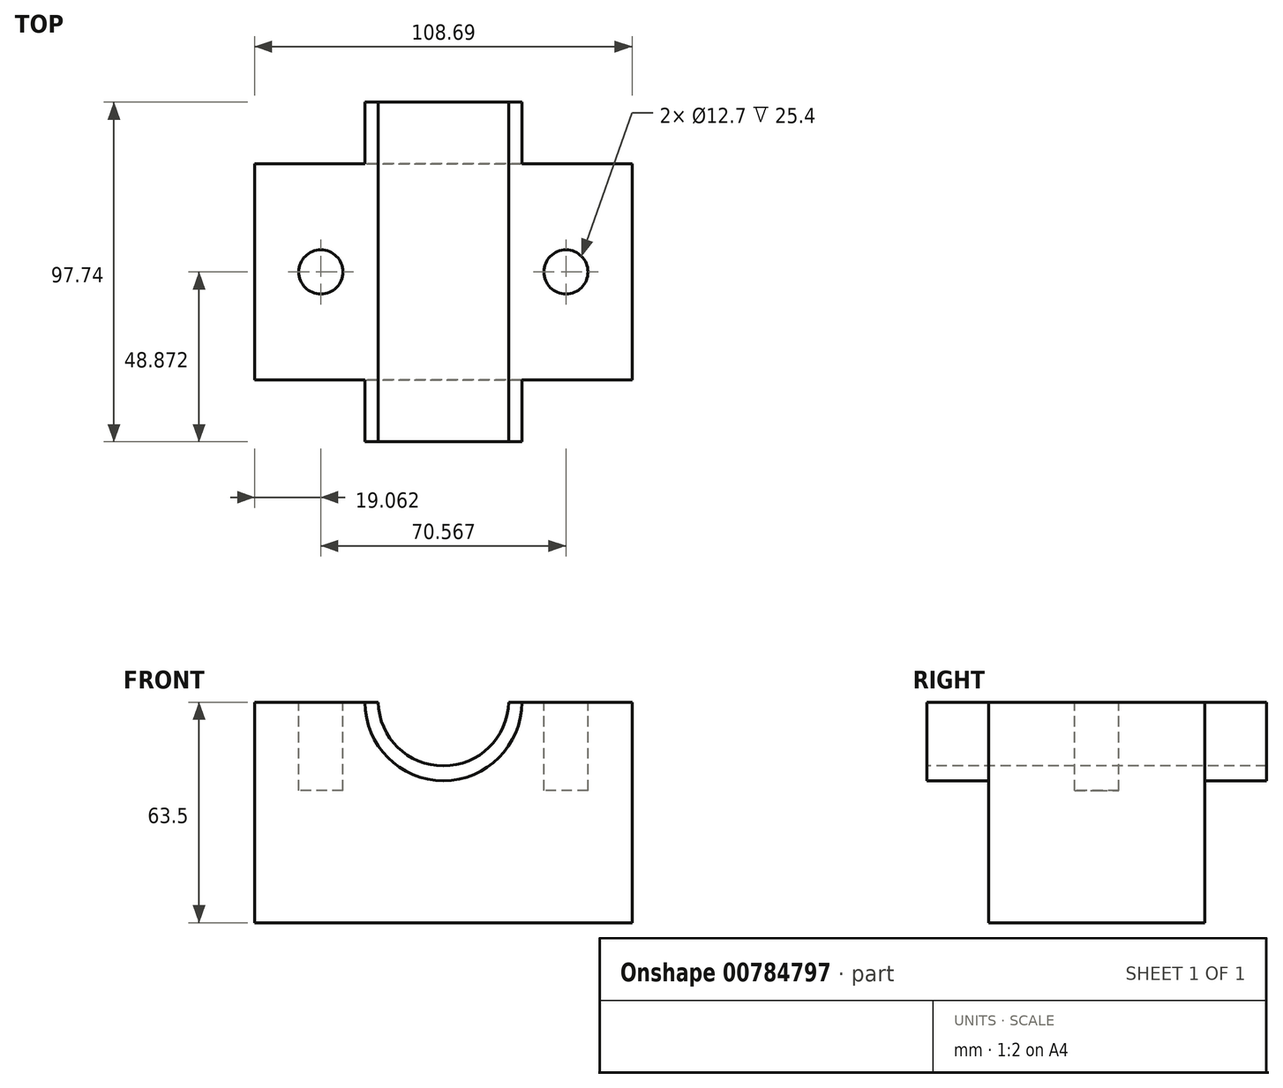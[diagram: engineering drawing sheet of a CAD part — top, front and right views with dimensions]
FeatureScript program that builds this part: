
annotation { "Feature Type Name" : "Feature", "Feature Type Description" : "" }
export const myFeature = defineFeature(function(context is Context, id is Id, definition is map)
    precondition{}
    {
        {
            var Q0;
            Q0=qCreatedBy(makeId("Top.planeOp"),FACE);
            var sketch = newSketch(context, id + "F0", { "sketchPlane" : qUnion([Q0])});
            skLineSegment(sketch, "E0.bottom", {"start": v(-52.9, 29.04) * mm, "end": v(55.8, 29.04) * mm});
            skLineSegment(sketch, "E0.top", {"start": v(-52.9, -33.14) * mm, "end": v(55.8, -33.14) * mm});
            skLineSegment(sketch, "E0.left", {"start": v(-52.9, 29.04) * mm, "end": v(-52.9, -33.14) * mm});
            skLineSegment(sketch, "E0.right", {"start": v(55.8, 29.04) * mm, "end": v(55.8, -33.14) * mm});
            skSolve(sketch);
        }
        {
            var Q0;
            Q0=makeQuery(id+"F0.imprint","IMPRINT",FACE,{"disambiguationData":[TD([[makeQuery(id+"F0.imprint","IMPRINT",EDGE,{"derivedFrom":sQuery(id+"F0.wireOp",EDGE,"E0.bottom")}),-1.0]])]});
            extrude(context, id + "F1", {"entities" : qUnion([Q0]), "depth" : 63.5 * mm, "offsetDistance" : 25.4 * mm});
        }
        {
            var Q0;
            Q0=makeQuery(id+"F1.opExtrude","CAP_FACE",FACE,{"disambiguationData":[OSD([sQuery(id+"F0.wireOp",EDGE,"E0.bottom"),sQuery(id+"F0.wireOp",EDGE,"E0.top"),sQuery(id+"F0.wireOp",EDGE,"E0.left"),sQuery(id+"F0.wireOp",EDGE,"E0.right")])],"isStart":false});
            var sketch = newSketch(context, id + "F2", { "sketchPlane" : qUnion([Q0])});
            skLineSegment(sketch, "E1", {"start": v(-52.9, -2.05) * mm, "end": v(-40.19, -2.05) * mm, "construction": true});
            skCircle(sketch, "E2", {"center": v(-33.84, -2.05) * mm, "radius": 6.35 * mm});
            skCircle(sketch, "E3", {"center": v(36.73, -2.05) * mm, "radius": 6.35 * mm});
            skLineSegment(sketch, "E4.trimOffspring", {"start": v(-33.84, -2.05) * mm, "end": v(36.73, -2.05) * mm, "construction": true});
            skLineSegment(sketch, "E5.trimOffspring", {"start": v(43.08, -2.05) * mm, "end": v(55.8, -2.05) * mm, "construction": true});
            skSolve(sketch);
        }
        {
            var Q0;
            Q0=makeQuery(id+"F2.imprint","IMPRINT",FACE,{"disambiguationData":[TD([[makeQuery(id+"F2.imprint","IMPRINT",EDGE,{"derivedFrom":sQuery(id+"F2.wireOp",EDGE,"E2")}),1.0]])]});
            var Q1;
            Q1=makeQuery(id+"F2.imprint","IMPRINT",FACE,{"disambiguationData":[TD([[makeQuery(id+"F2.imprint","IMPRINT",EDGE,{"derivedFrom":sQuery(id+"F2.wireOp",EDGE,"E3")}),1.0]])]});
            extrude(context, id + "F3", {"entities" : qUnion([Q0, Q1]), "operationType" : NewBodyOperationType.REMOVE, "oppositeDirection" : true, "depth" : 25.4 * mm, "offsetDistance" : 25.4 * mm});
        }
        {
            var Q0;
            Q0=makeQuery(id+"F1.opExtrude","CAP_FACE",FACE,{"disambiguationData":[OSD([sQuery(id+"F0.wireOp",EDGE,"E0.bottom"),sQuery(id+"F0.wireOp",EDGE,"E0.top"),sQuery(id+"F0.wireOp",EDGE,"E0.left"),sQuery(id+"F0.wireOp",EDGE,"E0.right")])],"isStart":false});
            var sketch = newSketch(context, id + "F4", { "sketchPlane" : qUnion([Q0])});
            skLineSegment(sketch, "E6", {"start": v(-21.15, -33.14) * mm, "end": v(-21.15, 29.04) * mm});
            skLineSegment(sketch, "E7", {"start": v(-21.15, 29.04) * mm, "end": v(-21.15, 46.82) * mm});
            skLineSegment(sketch, "E8", {"start": v(-21.15, 46.82) * mm, "end": v(24.04, 46.82) * mm});
            skLineSegment(sketch, "E9", {"start": v(24.04, 46.82) * mm, "end": v(24.04, -50.92) * mm});
            skLineSegment(sketch, "E10", {"start": v(24.04, -50.92) * mm, "end": v(-21.15, -50.92) * mm});
            skLineSegment(sketch, "E11", {"start": v(-21.15, -50.92) * mm, "end": v(-21.15, -33.14) * mm});
            skSolve(sketch);
        }
        {
            var Q0;
            {var subQ0=sQuery(id+"F4.wireOp",EDGE,"E10");Q0=makeQuery(id+"F4.imprint","IMPRINT",FACE,{"disambiguationData":[TD([[makeQuery(id+"F4.imprint","IMPRINT",EDGE,{"derivedFrom":subQ0}),-1.0]])]});}
            var Q1;
            {var subQ0=sQuery(id+"F4.wireOp",EDGE,"E6");Q1=makeQuery(id+"F4.imprint","IMPRINT",FACE,{"disambiguationData":[TD([[makeQuery(id+"F4.imprint","IMPRINT",EDGE,{"derivedFrom":subQ0}),-1.0]])]});}
            var Q2;
            {var subQ0=sQuery(id+"F4.wireOp",EDGE,"E7");Q2=makeQuery(id+"F4.imprint","IMPRINT",FACE,{"disambiguationData":[TD([[makeQuery(id+"F4.imprint","IMPRINT",EDGE,{"derivedFrom":subQ0}),-1.0]])]});}
            extrude(context, id + "F5", {"entities" : qUnion([Q0, Q1, Q2]), "operationType" : NewBodyOperationType.ADD, "oppositeDirection" : true, "depth" : 25.4 * mm, "offsetDistance" : 25.4 * mm});
        }
        {
            var Q0;
            Q0=makeQuery(id+"F5.opExtrude","SWEPT_FACE",FACE,{"disambiguationData":[OSD([sQuery(id+"F4.wireOp",EDGE,"E10")])]});
            var sketch = newSketch(context, id + "F6", { "sketchPlane" : qUnion([Q0])});
            skArc(sketch, "E12", {"start": v(-21.15, 63.5) * mm, "mid": v(1.45, 40.9) * mm, "end": v(24.04, 63.5) * mm});
            skPoint(sketch, "E13", {"position": v(-17.34, 63.5) * mm});
            skPoint(sketch, "E14", {"position": v(20.23, 63.5) * mm});
            skArc(sketch, "E15", {"start": v(-17.34, 63.5) * mm, "mid": v(1.45, 45.17) * mm, "end": v(20.23, 63.5) * mm});
            skSolve(sketch);
        }
        {
            var Q0;
            Q0=makeQuery(id+"F6.imprint","IMPRINT",FACE,{"disambiguationData":[TD([[makeQuery(id+"F6.imprint","IMPRINT",EDGE,{"derivedFrom":sQuery(id+"F6.wireOp",EDGE,"E12")}),-1.0]])]});
            var Q1;
            Q1=makeQuery(id+"F1.opExtrude","SWEPT_FACE",FACE,{"disambiguationData":[OSD([sQuery(id+"F0.wireOp",EDGE,"E0.top")])]});
            extrude(context, id + "F7", {"entities" : qUnion([Q0]), "operationType" : NewBodyOperationType.REMOVE, "endBound" : BoundingType.UP_TO_SURFACE, "oppositeDirection" : true, "depth" : 25.4 * mm, "endBoundEntityFace" : qUnion([Q1]), "offsetDistance" : 25.4 * mm});
        }
        {
            var Q0;
            Q0=makeQuery(id+"F5.opExtrude","SWEPT_FACE",FACE,{"disambiguationData":[OSD([sQuery(id+"F4.wireOp",EDGE,"E10")])]});
            var sketch = newSketch(context, id + "F8", { "sketchPlane" : qUnion([Q0])});
            skPoint(sketch, "E16", {"position": v(-17.34, 63.5) * mm});
            skPoint(sketch, "E17", {"position": v(20.23, 63.5) * mm});
            skArc(sketch, "E18", {"start": v(-17.34, 63.5) * mm, "mid": v(1.45, 45.13) * mm, "end": v(20.23, 63.5) * mm});
            skSolve(sketch);
        }
        {
            var Q0;
            {var subQ0=sQuery(id+"F8.wireOp",EDGE,"E18");Q0=makeQuery(id+"F8.imprint","IMPRINT",FACE,{"disambiguationData":[TD([[makeQuery(id+"F8.imprint","IMPRINT",EDGE,{"derivedFrom":subQ0}),1.0]])]});}
            var Q1;
            Q1=makeQuery(id+"F5.opExtrude","SWEPT_FACE",FACE,{"disambiguationData":[OSD([sQuery(id+"F4.wireOp",EDGE,"E8")])]});
            extrude(context, id + "F9", {"entities" : qUnion([Q0]), "operationType" : NewBodyOperationType.REMOVE, "endBound" : BoundingType.UP_TO_SURFACE, "oppositeDirection" : true, "depth" : 25.4 * mm, "endBoundEntityFace" : qUnion([Q1]), "offsetDistance" : 25.4 * mm});
        }
        {
            var Q0;
            Q0=makeQuery(id+"F5.opExtrude","SWEPT_FACE",FACE,{"disambiguationData":[OSD([sQuery(id+"F4.wireOp",EDGE,"E8")])]});
            var sketch = newSketch(context, id + "F10", { "sketchPlane" : qUnion([Q0])});
            skArc(sketch, "E19", {"start": v(-24.04, 63.5) * mm, "mid": v(-1.45, 40.9) * mm, "end": v(21.15, 63.5) * mm});
            skSolve(sketch);
        }
        {
            var Q0;
            Q0=makeQuery(id+"F10.imprint","IMPRINT",FACE,{"disambiguationData":[TD([[makeQuery(id+"F10.imprint","IMPRINT",EDGE,{"derivedFrom":sQuery(id+"F10.wireOp",EDGE,"E19")}),-1.0]])]});
            var Q1;
            Q1=makeQuery(id+"F1.opExtrude","SWEPT_FACE",FACE,{"disambiguationData":[OSD([sQuery(id+"F0.wireOp",EDGE,"E0.bottom")])]});
            extrude(context, id + "F11", {"entities" : qUnion([Q0]), "operationType" : NewBodyOperationType.ADD, "endBound" : BoundingType.UP_TO_SURFACE, "oppositeDirection" : true, "depth" : 25.4 * mm, "endBoundEntityFace" : qUnion([Q1]), "offsetDistance" : 25.4 * mm});
        }
        {
            var Q0;
            Q0=makeQuery(id+"F5.opExtrude","SWEPT_FACE",FACE,{"disambiguationData":[OSD([sQuery(id+"F4.wireOp",EDGE,"E8")])]});
            var sketch = newSketch(context, id + "F12", { "sketchPlane" : qUnion([Q0])});
            skArc(sketch, "E20", {"start": v(-24.04, 63.5) * mm, "mid": v(-1.45, 40.9) * mm, "end": v(21.15, 63.5) * mm});
            skSolve(sketch);
        }
        {
            var Q0;
            Q0=makeQuery(id+"F12.imprint","IMPRINT",FACE,{"disambiguationData":[TD([[makeQuery(id+"F12.imprint","IMPRINT",EDGE,{"derivedFrom":sQuery(id+"F12.wireOp",EDGE,"E20")}),-1.0]])]});
            var Q1;
            Q1=makeQuery(id+"F1.opExtrude","SWEPT_FACE",FACE,{"disambiguationData":[OSD([sQuery(id+"F0.wireOp",EDGE,"E0.bottom")])]});
            extrude(context, id + "F13", {"entities" : qUnion([Q0]), "operationType" : NewBodyOperationType.REMOVE, "endBound" : BoundingType.UP_TO_SURFACE, "oppositeDirection" : true, "depth" : 25.4 * mm, "endBoundEntityFace" : qUnion([Q1]), "offsetDistance" : 25.4 * mm});
        }
    });
